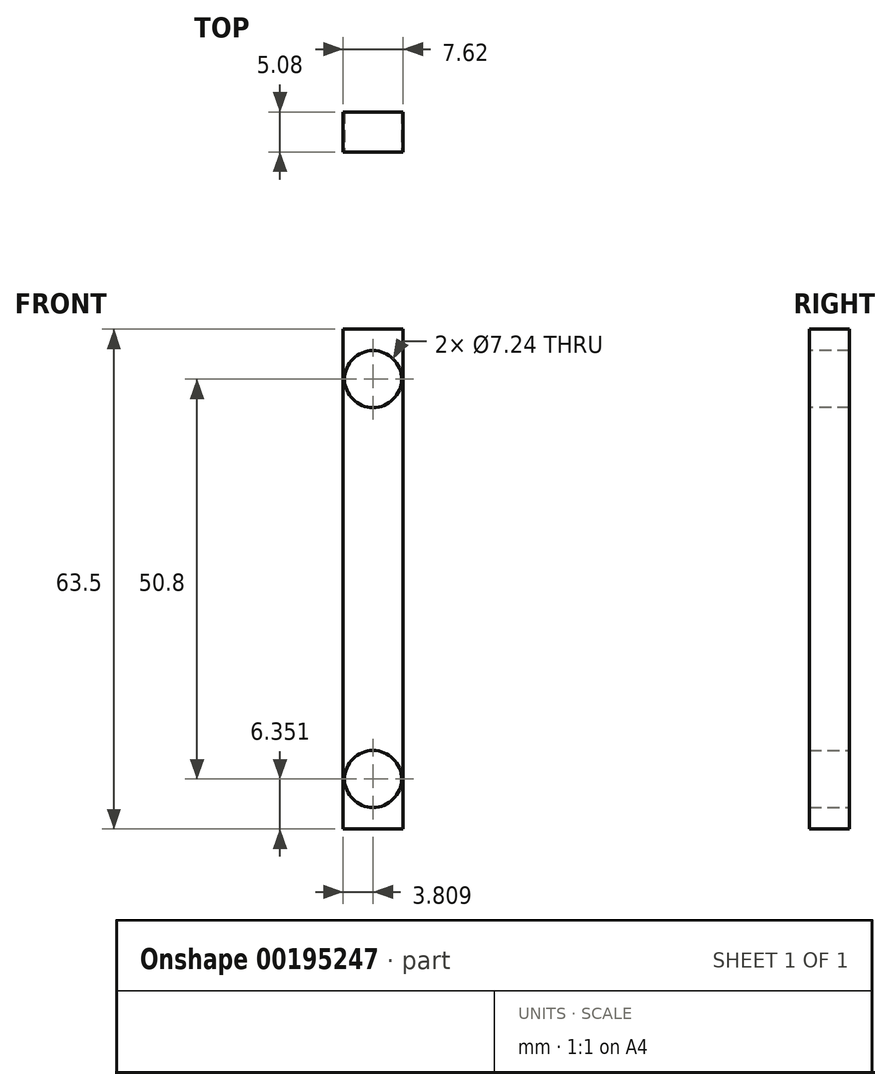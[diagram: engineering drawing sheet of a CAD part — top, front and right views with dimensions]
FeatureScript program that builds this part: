
annotation { "Feature Type Name" : "Feature", "Feature Type Description" : "" }
export const myFeature = defineFeature(function(context is Context, id is Id, definition is map)
    precondition{}
    {
        {
            var Q0;
            Q0=qCreatedBy(makeId("Front.planeOp"),FACE);
            var sketch = newSketch(context, id + "F0", { "sketchPlane" : qUnion([Q0])});
            skLineSegment(sketch, "E0.bottom", {"start": v(-7.57, 54.72) * mm, "end": v(0.05, 54.72) * mm});
            skLineSegment(sketch, "E0.top", {"start": v(-7.57, -8.78) * mm, "end": v(0.05, -8.78) * mm});
            skLineSegment(sketch, "E0.left", {"start": v(-7.57, 54.72) * mm, "end": v(-7.57, -8.78) * mm});
            skLineSegment(sketch, "E0.right", {"start": v(0.05, 54.72) * mm, "end": v(0.05, -8.78) * mm});
            skSolve(sketch);
        }
        {
            var Q0;
            Q0=qSketchRegion(id+"F0",true);
            extrude(context, id + "F1", {"entities" : qUnion([Q0]), "depth" : 5.08 * mm});
        }
        {
            var Q0;
            Q0=makeQuery(id+"F1.opExtrude","CAP_FACE",FACE,{"disambiguationData":[OSD([sQuery(id+"F0.wireOp",EDGE,"E0.bottom"),sQuery(id+"F0.wireOp",EDGE,"E0.top"),sQuery(id+"F0.wireOp",EDGE,"E0.left"),sQuery(id+"F0.wireOp",EDGE,"E0.right")])],"isStart":false});
            var sketch = newSketch(context, id + "F2", { "sketchPlane" : qUnion([Q0])});
            skCircle(sketch, "E1", {"center": v(-3.76, 48.37) * mm, "radius": 3.62 * mm, "construction": true});
            skPoint(sketch, "E1.centerSnap0", {"position": v(-3.76, 54.72) * mm});
            skSolve(sketch);
        }
        {
            var Q0;
            Q0=qCreatedBy(makeId("Front.planeOp"),FACE);
            var sketch = newSketch(context, id + "F3", { "sketchPlane" : qUnion([Q0])});
            skCircle(sketch, "E2", {"center": v(-3.76, -2.43) * mm, "radius": 3.62 * mm, "construction": true});
            skSolve(sketch);
        }
        {
            var Q0;
            Q0=sQuery(id+"F2.wireOp",VERTEX,"E1.center");
            var Q1;
            Q1=makeQuery(id+"F1.opExtrude","SWEPT_BODY",BODY,{"disambiguationData":[OSD([sQuery(id+"F0.wireOp",EDGE,"E0.bottom"),sQuery(id+"F0.wireOp",EDGE,"E0.top"),sQuery(id+"F0.wireOp",EDGE,"E0.left"),sQuery(id+"F0.wireOp",EDGE,"E0.right")])]});
            hole(context, id + "F4", {"style" : HoleStyle.SIMPLE, "endStyle" : HoleEndStyle.THROUGH, "holeDiameter" : 7.24 * mm, "locations" : qUnion([Q0]), "scope" : qUnion([Q1]), "isTappedThrough" : true});
        }
        {
            var Q0;
            Q0=sQuery(id+"F3.wireOp",VERTEX,"E2.center");
            var Q1;
            Q1=makeQuery(id+"F1.opExtrude","SWEPT_BODY",BODY,{"disambiguationData":[OSD([sQuery(id+"F0.wireOp",EDGE,"E0.bottom"),sQuery(id+"F0.wireOp",EDGE,"E0.top"),sQuery(id+"F0.wireOp",EDGE,"E0.left"),sQuery(id+"F0.wireOp",EDGE,"E0.right")])]});
            hole(context, id + "F5", {"style" : HoleStyle.SIMPLE, "endStyle" : HoleEndStyle.THROUGH, "oppositeDirection" : true, "holeDiameter" : 7.24 * mm, "locations" : qUnion([Q0]), "scope" : qUnion([Q1]), "isTappedThrough" : true});
        }
    });
